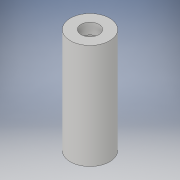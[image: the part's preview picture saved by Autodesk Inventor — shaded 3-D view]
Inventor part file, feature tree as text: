
AUTODESK INVENTOR PART (.ipt)
format: ipt  version: 2018 (Build 220112000, 112)  size: 104,960 bytes
history: native  units: in
note: dims shown in document units (in); Inventor stores cm internally (conversion verified against a paired STEP export)
features: extrude x2, sketch x2
ambient origin geometry x8: Origin, YZ Plane, XZ Plane, XY Plane, X Axis, Y Axis, Z Axis, Center Point
bodies: Solid1 (feature_tree)
feature tree (4):
  extrude  "Extrusion1"  Depth=0.325in
  extrude  "Extrusion2"  Depth=1.7in
  sketch  "Sketch1"  dims[d0=0.71in d1=0.325in]
  sketch  "Sketch2"  dims[d2=0.2in d3=0.0in d4=0.45in d5=1.7in d6=0.0in]
